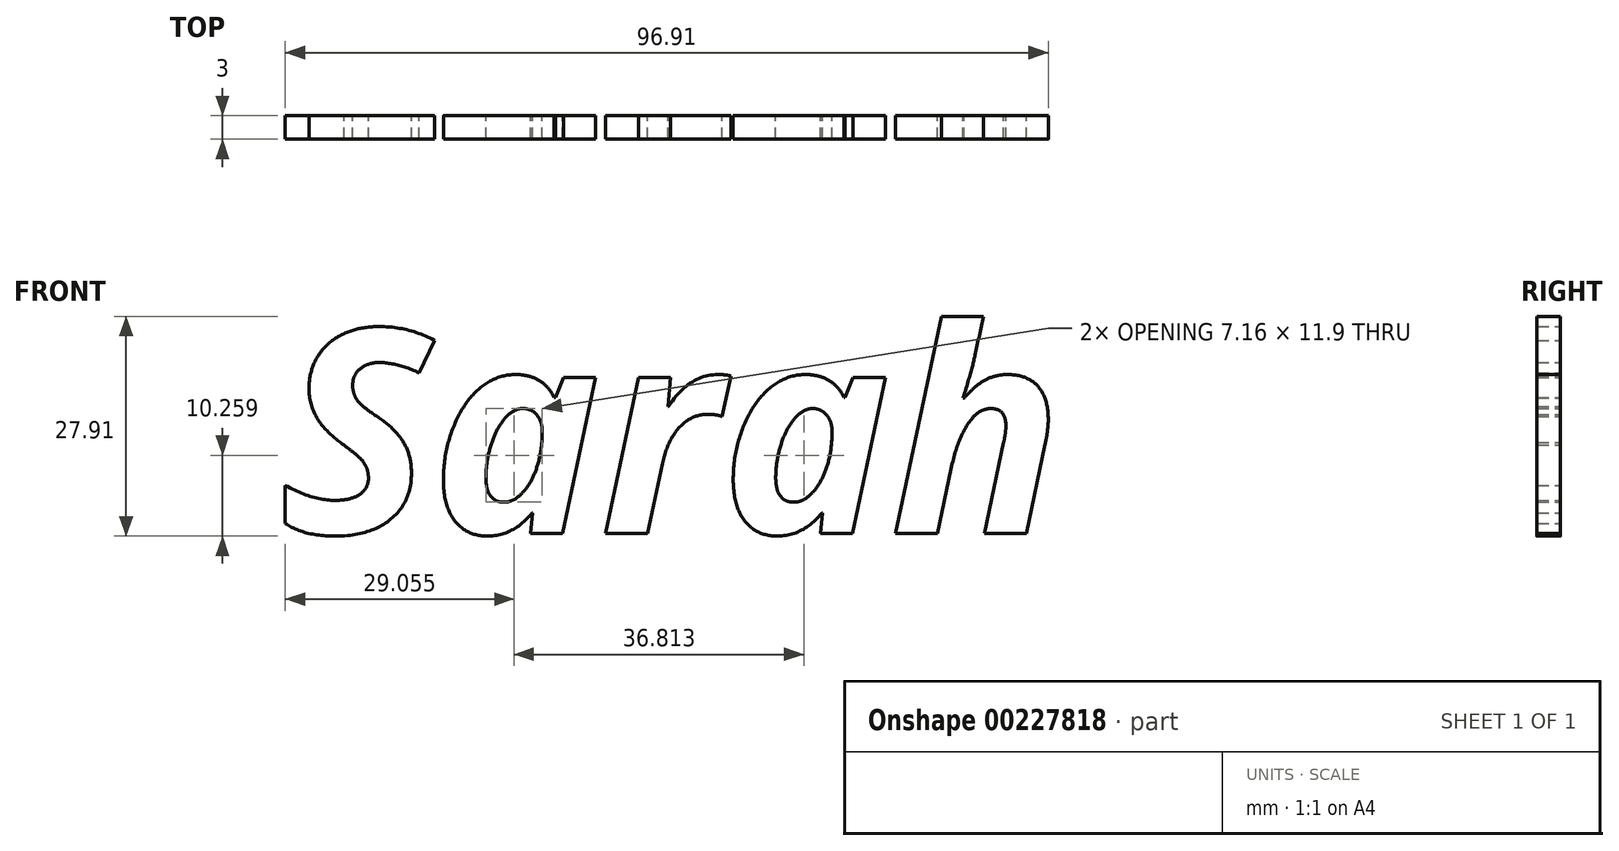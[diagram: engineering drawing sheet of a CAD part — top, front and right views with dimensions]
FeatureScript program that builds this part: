
annotation { "Feature Type Name" : "Feature", "Feature Type Description" : "" }
export const myFeature = defineFeature(function(context is Context, id is Id, definition is map)
    precondition{}
    {
        {
            var Q0;
            Q0=qCreatedBy(makeId("Front.planeOp"),FACE);
            var sketch = newSketch(context, id + "F0", { "sketchPlane" : qUnion([Q0])});
            skText(sketch, "E0", { "text": "Sarah", "fontName": "OpenSans-BoldItalic.ttf"});
            skLineSegment(sketch, "E1", {"start": v(-99.79, 19.6) * mm, "end": v(-5.62, 19.6) * mm});
            skLineSegment(sketch, "E2", {"start": v(-99.79, 21.19) * mm, "end": v(-99.79, 19.6) * mm});
            skLineSegment(sketch, "E3", {"start": v(-5.62, 19.95) * mm, "end": v(-5.62, 19.6) * mm});
            const initialGuessF0  = {"E0": [-0.10051, 0.01995, 1, 0, 0.02611]};
            skSetInitialGuess(sketch, initialGuessF0);
            skSolve(sketch);
        }
        {
            var Q0;
            Q0 = qSketchRegion(id + "F0", true);
            extrude(context, id + "F1", {"entities" : qUnion([Q0]), "depth" : 3 * mm});
        }
    });
